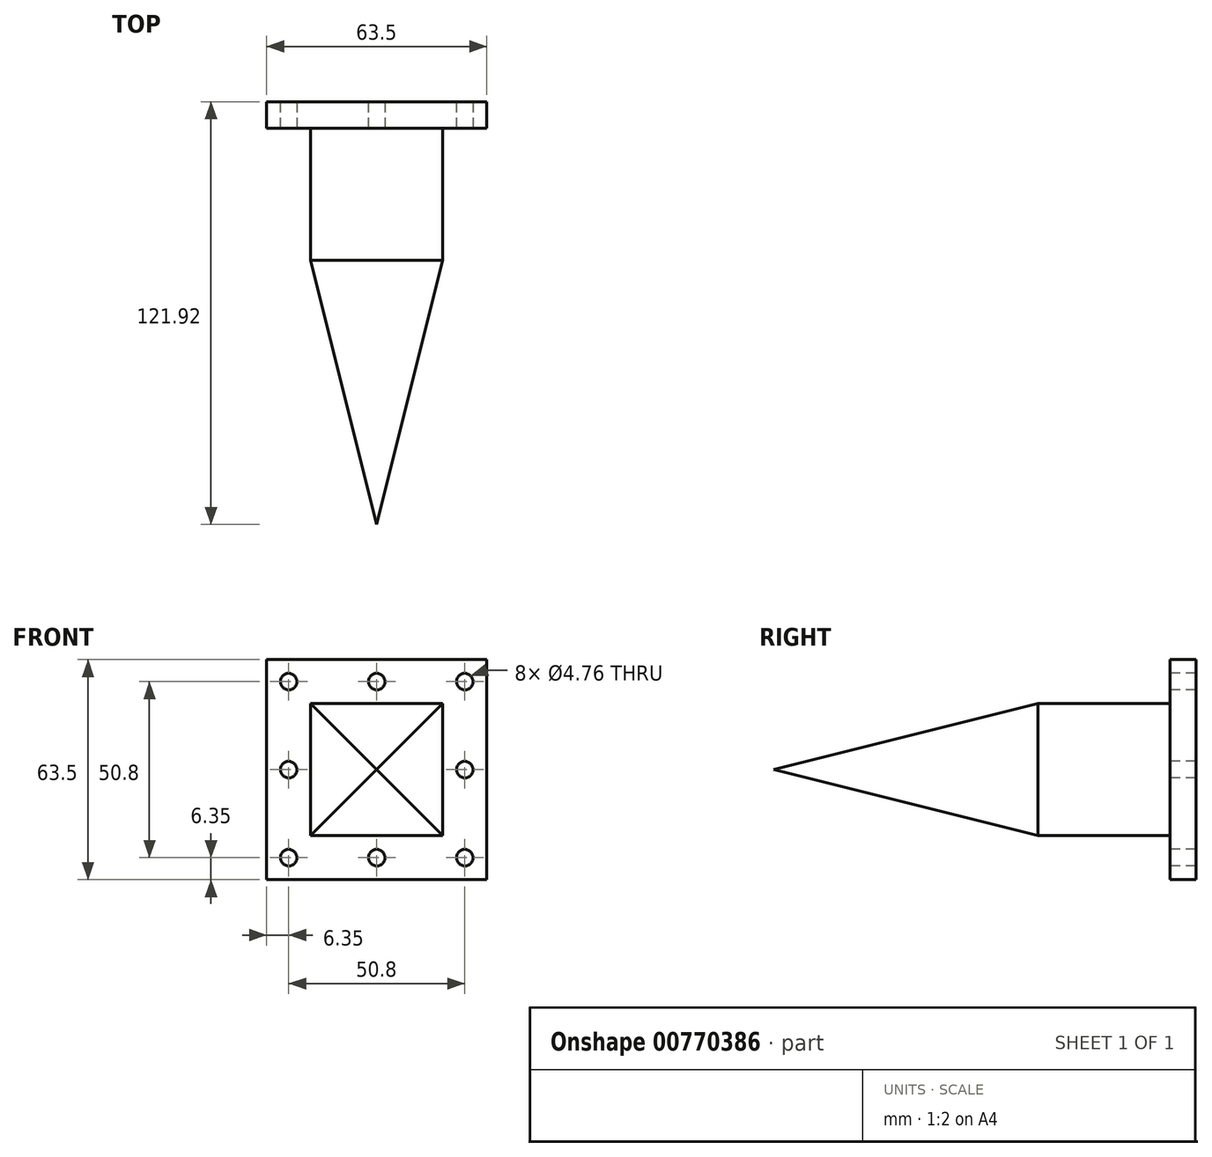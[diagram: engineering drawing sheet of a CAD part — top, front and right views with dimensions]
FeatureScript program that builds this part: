
annotation { "Feature Type Name" : "Feature", "Feature Type Description" : "" }
export const myFeature = defineFeature(function(context is Context, id is Id, definition is map)
    precondition{}
    {
        {
            var Q0;
            Q0=qCreatedBy(makeId("Front.planeOp"),FACE);
            var sketch = newSketch(context, id + "F0", { "sketchPlane" : qUnion([Q0])});
            skLineSegment(sketch, "E0.bottom", {"start": v(0, 0) * mm, "end": v(63.5, 0) * mm});
            skLineSegment(sketch, "E0.top", {"start": v(0, -63.5) * mm, "end": v(63.5, -63.5) * mm});
            skLineSegment(sketch, "E0.left", {"start": v(0, 0) * mm, "end": v(0, -63.5) * mm});
            skLineSegment(sketch, "E0.right", {"start": v(63.5, 0) * mm, "end": v(63.5, -63.5) * mm});
            skSolve(sketch);
        }
        {
            var Q0;
            Q0=makeQuery(id+"F0.imprint","IMPRINT",FACE,{"disambiguationData":[TD([[makeQuery(id+"F0.imprint","IMPRINT",EDGE,{"derivedFrom":sQuery(id+"F0.wireOp",EDGE,"E0.bottom")}),-1.0]])]});
            extrude(context, id + "F1", {"entities" : qUnion([Q0]), "depth" : 7.62 * mm, "offsetDistance" : 25.4 * mm});
        }
        {
            var Q0;
            Q0=makeQuery(id+"F1.opExtrude","CAP_FACE",FACE,{"disambiguationData":[OSD([sQuery(id+"F0.wireOp",EDGE,"E0.bottom"),sQuery(id+"F0.wireOp",EDGE,"E0.top"),sQuery(id+"F0.wireOp",EDGE,"E0.left"),sQuery(id+"F0.wireOp",EDGE,"E0.right")])],"isStart":false});
            var sketch = newSketch(context, id + "F2", { "sketchPlane" : qUnion([Q0])});
            skLineSegment(sketch, "E1", {"start": v(31.75, 0) * mm, "end": v(31.75, -31.75) * mm});
            skLineSegment(sketch, "E2.bottom", {"start": v(50.8, -50.8) * mm, "end": v(12.7, -50.8) * mm});
            skLineSegment(sketch, "E2.top", {"start": v(50.8, -12.7) * mm, "end": v(12.7, -12.7) * mm});
            skLineSegment(sketch, "E2.left", {"start": v(50.8, -50.8) * mm, "end": v(50.8, -12.7) * mm});
            skLineSegment(sketch, "E2.right", {"start": v(12.7, -50.8) * mm, "end": v(12.7, -12.7) * mm});
            skPoint(sketch, "E2.middle", {"position": v(31.75, -31.75) * mm});
            skSolve(sketch);
        }
        {
            var Q0;
            Q0=makeQuery(id+"F2.imprint","IMPRINT",FACE,{"disambiguationData":[TD([[makeQuery(id+"F2.imprint","IMPRINT",EDGE,{"derivedFrom":sQuery(id+"F2.wireOp",EDGE,"E2.bottom")}),-1.0]])]});
            extrude(context, id + "F3", {"entities" : qUnion([Q0]), "operationType" : NewBodyOperationType.ADD, "depth" : 114.3 * mm, "offsetDistance" : 25.4 * mm});
        }
        {
            var Q0;
            Q0=makeQuery(id+"F3.opExtrude","CAP_FACE",FACE,{"disambiguationData":[OSD([sQuery(id+"F2.wireOp",EDGE,"E2.bottom"),sQuery(id+"F2.wireOp",EDGE,"E2.top"),sQuery(id+"F2.wireOp",EDGE,"E2.left"),sQuery(id+"F2.wireOp",EDGE,"E2.right")])],"isStart":false});
            chamfer(context, id + "F4", {"entities" : qUnion([Q0]), "chamferType" : ChamferType.TWO_OFFSETS, "width1" : 76.2 * mm, "oppositeDirection" : false, "width2" : 19.05 * mm, "tangentPropagation" : true});
        }
        {
            var Q0;
            Q0=makeQuery(id+"F1.opExtrude","CAP_FACE",FACE,{"disambiguationData":[OSD([sQuery(id+"F0.wireOp",EDGE,"E0.bottom"),sQuery(id+"F0.wireOp",EDGE,"E0.top"),sQuery(id+"F0.wireOp",EDGE,"E0.left"),sQuery(id+"F0.wireOp",EDGE,"E0.right")])],"isStart":false});
            var sketch = newSketch(context, id + "F5", { "sketchPlane" : qUnion([Q0])});
            skLineSegment(sketch, "E3", {"start": v(0, 0) * mm, "end": v(0, -6.35) * mm, "construction": true});
            skLineSegment(sketch, "E4", {"start": v(0, -6.35) * mm, "end": v(6.35, -6.35) * mm, "construction": true});
            skCircle(sketch, "E5", {"center": v(6.35, -6.35) * mm, "radius": 2.38 * mm});
            skCircle(sketch, "E6.0.1.0", {"center": v(6.35, -31.75) * mm, "radius": 2.38 * mm});
            skCircle(sketch, "E6.0.2.0", {"center": v(6.35, -57.15) * mm, "radius": 2.38 * mm});
            skCircle(sketch, "E6.1.0.0", {"center": v(31.75, -6.35) * mm, "radius": 2.38 * mm});
            skCircle(sketch, "E6.1.1.0", {"center": v(31.75, -31.75) * mm, "radius": 2.38 * mm});
            skCircle(sketch, "E6.1.2.0", {"center": v(31.75, -57.15) * mm, "radius": 2.38 * mm});
            skCircle(sketch, "E6.2.0.0", {"center": v(57.15, -6.35) * mm, "radius": 2.38 * mm});
            skCircle(sketch, "E6.2.1.0", {"center": v(57.15, -31.75) * mm, "radius": 2.38 * mm});
            skCircle(sketch, "E6.2.2.0", {"center": v(57.15, -57.15) * mm, "radius": 2.38 * mm});
            skLineSegment(sketch, "E6.direction1", {"start": v(6.35, -6.35) * mm, "end": v(31.75, -6.35) * mm, "construction": true});
            skLineSegment(sketch, "E6.direction2", {"start": v(6.35, -6.35) * mm, "end": v(6.35, -31.75) * mm, "construction": true});
            skSolve(sketch);
        }
        {
            var Q0;
            Q0=makeQuery(id+"F5.imprint","IMPRINT",FACE,{"disambiguationData":[TD([[makeQuery(id+"F5.imprint","IMPRINT",EDGE,{"derivedFrom":sQuery(id+"F5.wireOp",EDGE,"E5")}),-1.0]])]});
            var sketch = newSketch(context, id + "F6", { "sketchPlane" : qUnion([Q0])});
            skSolve(sketch);
        }
        {
            var Q0;
            Q0 = qSketchRegion(id + "F6", true);
            var Q1;
            Q1=makeQuery(id+"F5.imprint","IMPRINT",FACE,{"disambiguationData":[TD([[makeQuery(id+"F5.imprint","IMPRINT",EDGE,{"derivedFrom":sQuery(id+"F5.wireOp",EDGE,"E5")}),1.0]])]});
            extrude(context, id + "F7", {"entities" : qUnion([Q0, Q1]), "operationType" : NewBodyOperationType.REMOVE, "oppositeDirection" : true, "depth" : 25.4 * mm, "offsetDistance" : 25.4 * mm});
        }
        {
            var Q0;
            Q0=makeQuery(id+"F5.imprint","IMPRINT",FACE,{"disambiguationData":[TD([[makeQuery(id+"F5.imprint","IMPRINT",EDGE,{"derivedFrom":sQuery(id+"F5.wireOp",EDGE,"E5")}),-1.0]])]});
            var sketch = newSketch(context, id + "F8", { "sketchPlane" : qUnion([Q0])});
            skSolve(sketch);
        }
        {
            var Q0;
            Q0 = qSketchRegion(id + "F8", true);
            var Q1;
            Q1=makeQuery(id+"F5.imprint","IMPRINT",FACE,{"disambiguationData":[TD([[makeQuery(id+"F5.imprint","IMPRINT",EDGE,{"derivedFrom":sQuery(id+"F5.wireOp",EDGE,"E6.0.1.0")}),1.0]])]});
            var Q2;
            Q2=makeQuery(id+"F5.imprint","IMPRINT",FACE,{"disambiguationData":[TD([[makeQuery(id+"F5.imprint","IMPRINT",EDGE,{"derivedFrom":sQuery(id+"F5.wireOp",EDGE,"E6.0.2.0")}),1.0]])]});
            var Q3;
            Q3=makeQuery(id+"F5.imprint","IMPRINT",FACE,{"disambiguationData":[TD([[makeQuery(id+"F5.imprint","IMPRINT",EDGE,{"derivedFrom":sQuery(id+"F5.wireOp",EDGE,"E6.1.2.0")}),1.0]])]});
            var Q4;
            Q4=makeQuery(id+"F5.imprint","IMPRINT",FACE,{"disambiguationData":[TD([[makeQuery(id+"F5.imprint","IMPRINT",EDGE,{"derivedFrom":sQuery(id+"F5.wireOp",EDGE,"E6.2.2.0")}),1.0]])]});
            var Q5;
            Q5=makeQuery(id+"F5.imprint","IMPRINT",FACE,{"disambiguationData":[TD([[makeQuery(id+"F5.imprint","IMPRINT",EDGE,{"derivedFrom":sQuery(id+"F5.wireOp",EDGE,"E6.2.1.0")}),1.0]])]});
            var Q6;
            Q6=makeQuery(id+"F5.imprint","IMPRINT",FACE,{"disambiguationData":[TD([[makeQuery(id+"F5.imprint","IMPRINT",EDGE,{"derivedFrom":sQuery(id+"F5.wireOp",EDGE,"E6.2.0.0")}),1.0]])]});
            var Q7;
            Q7=makeQuery(id+"F5.imprint","IMPRINT",FACE,{"disambiguationData":[TD([[makeQuery(id+"F5.imprint","IMPRINT",EDGE,{"derivedFrom":sQuery(id+"F5.wireOp",EDGE,"E6.1.0.0")}),1.0]])]});
            extrude(context, id + "F9", {"entities" : qUnion([Q0, Q1, Q2, Q3, Q4, Q5, Q6, Q7]), "operationType" : NewBodyOperationType.REMOVE, "oppositeDirection" : true, "depth" : 25.4 * mm, "offsetDistance" : 25.4 * mm});
        }
    });
